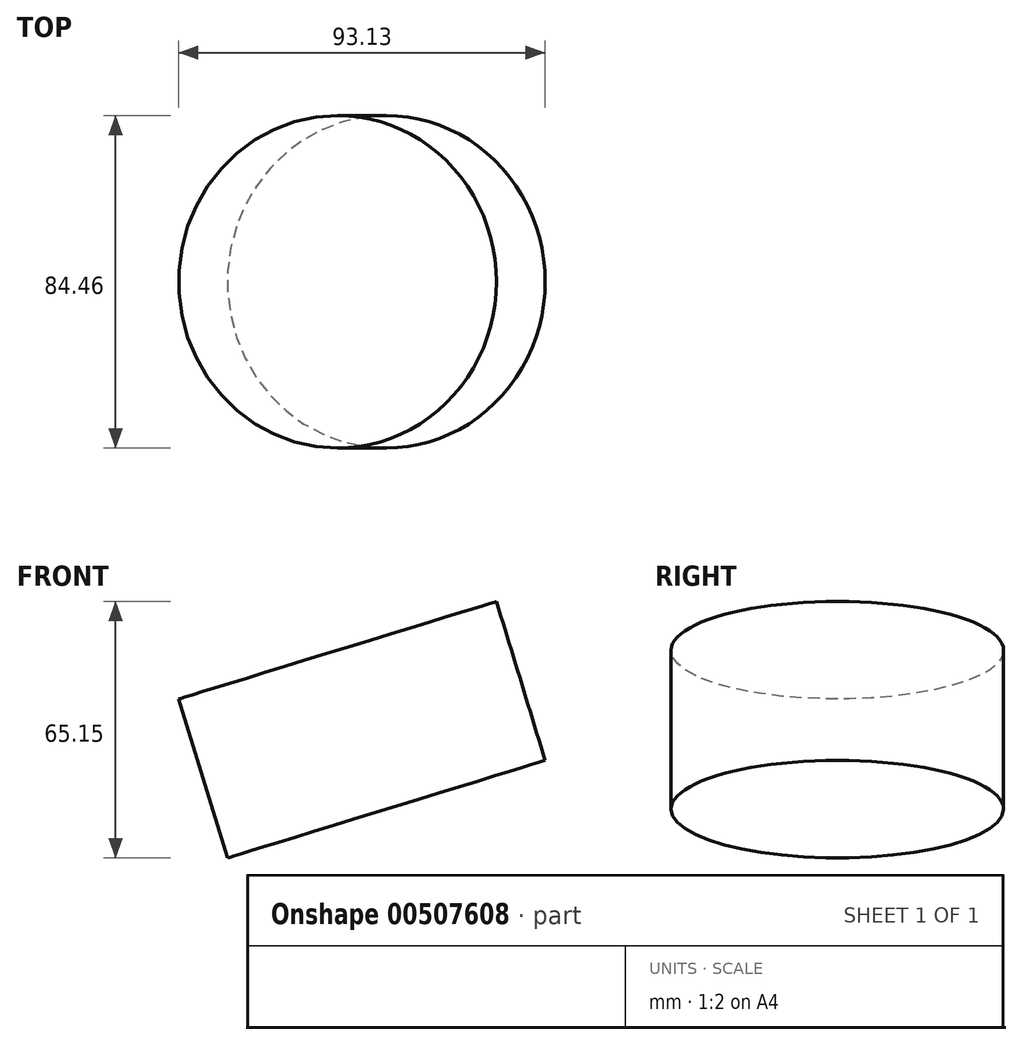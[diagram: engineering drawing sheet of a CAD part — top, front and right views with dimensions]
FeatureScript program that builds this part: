
annotation { "Feature Type Name" : "Feature", "Feature Type Description" : "" }
export const myFeature = defineFeature(function(context is Context, id is Id, definition is map)
    precondition{}
    {
        {
            var Q0;
            Q0=qCreatedBy(makeId("Front.planeOp"),FACE);
            var sketch = newSketch(context, id + "F0", { "sketchPlane" : qUnion([Q0])});
            skCircle(sketch, "E0.cCircle", {"center": v(0, 0) * mm, "radius": 29.86 * mm, "construction": true});
            skLineSegment(sketch, "E0.0", {"start": v(-14, -26.38) * mm, "end": v(-26.38, 14) * mm});
            skLineSegment(sketch, "E0.1", {"start": v(-26.38, 14) * mm, "end": v(14, 26.38) * mm});
            skLineSegment(sketch, "E0.2", {"start": v(14, 26.38) * mm, "end": v(26.38, -14) * mm});
            skLineSegment(sketch, "E0.3", {"start": v(26.38, -14) * mm, "end": v(-14, -26.38) * mm});
            skSolve(sketch);
        }
        {
            var Q0;
            Q0 = qSketchRegion(id + "F0", true);
            var Q1;
            Q1=sQuery(id+"F0.wireOp",EDGE,"E0.2");
            revolve(context, id + "F1", {"entities" : qUnion([Q0]), "axis" : qUnion([Q1]), "revolveType" : RevolveType.FULL});
        }
    });
